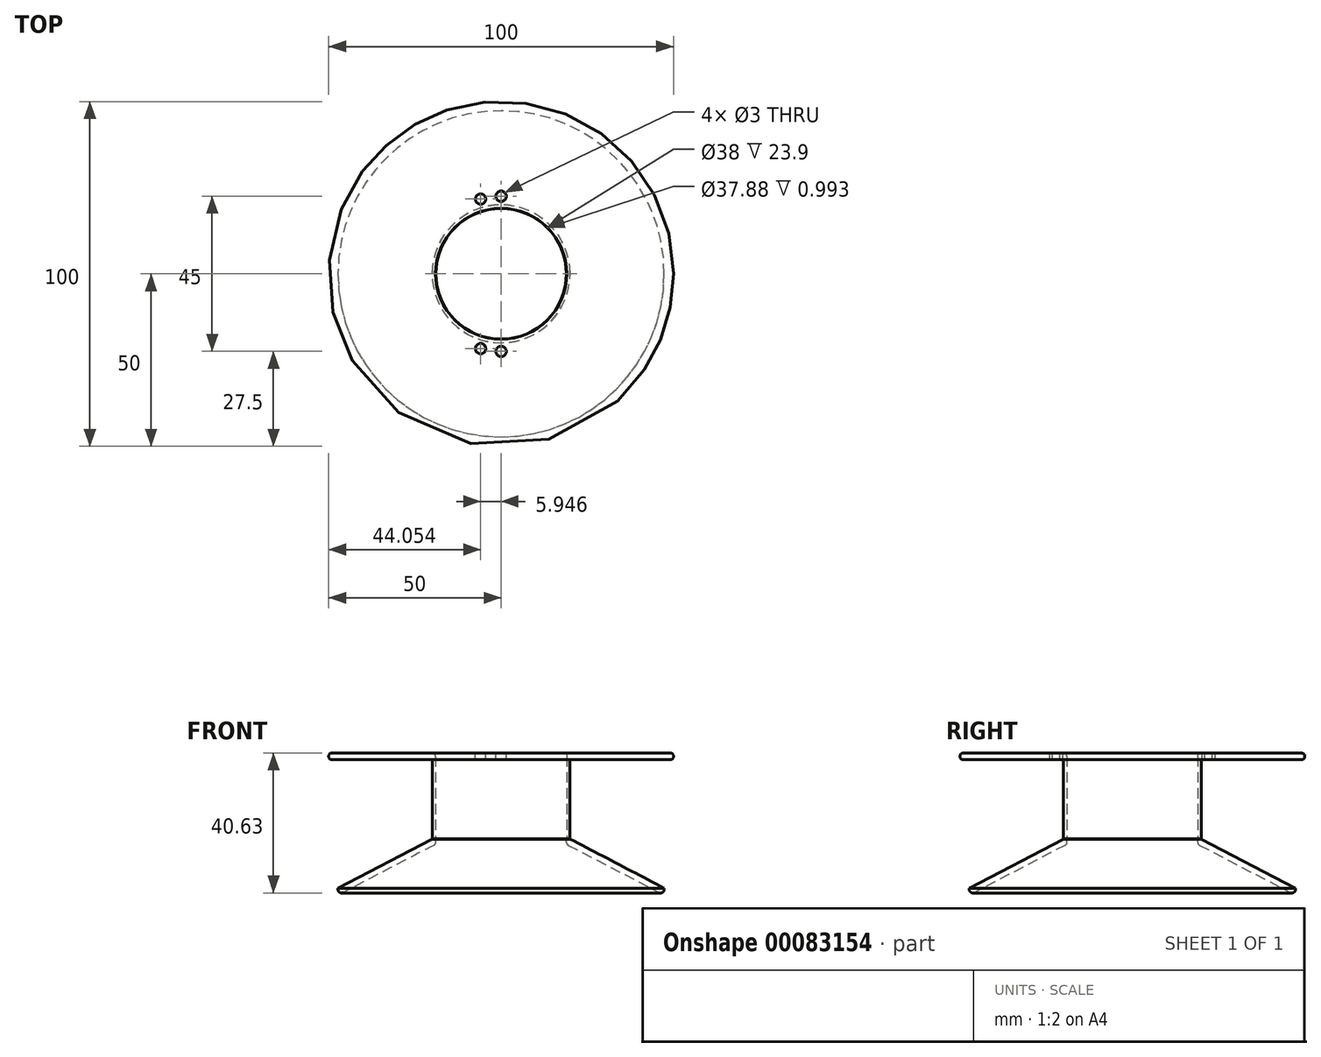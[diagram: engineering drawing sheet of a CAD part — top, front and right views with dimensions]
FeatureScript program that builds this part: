
annotation { "Feature Type Name" : "Feature", "Feature Type Description" : "" }
export const myFeature = defineFeature(function(context is Context, id is Id, definition is map)
    precondition{}
    {
        {
            var Q0;
            Q0=qCreatedBy(makeId("Top.planeOp"),FACE);
            var sketch = newSketch(context, id + "F0", { "sketchPlane" : qUnion([Q0])});
            skCircle(sketch, "E0", {"center": v(0, 0) * mm, "radius": 20 * mm});
            skCircle(sketch, "E1", {"center": v(0, 0) * mm, "radius": 19 * mm});
            skSolve(sketch);
        }
        {
            var Q0;
            Q0=makeQuery(id+"F0.imprint","IMPRINT",FACE,{"disambiguationData":[TD([[makeQuery(id+"F0.imprint","IMPRINT",EDGE,{"derivedFrom":sQuery(id+"F0.wireOp",EDGE,"E0")}),1.0]])]});
            extrude(context, id + "F1", {"entities" : qUnion([Q0]), "endBound" : BoundingType.SYMMETRIC, "depth" : 25 * mm});
        }
        {
            var Q0;
            Q0=makeQuery(id+"F1.opExtrude","CAP_FACE",FACE,{"disambiguationData":[OSD([sQuery(id+"F0.wireOp",EDGE,"E0"),sQuery(id+"F0.wireOp",EDGE,"E1")])],"isStart":false});
            var sketch = newSketch(context, id + "F2", { "sketchPlane" : qUnion([Q0])});
            skCircle(sketch, "E2", {"center": v(0, 0) * mm, "radius": 50 * mm});
            skCircle(sketch, "E3", {"center": v(0, 22.5) * mm, "radius": 1.5 * mm});
            skCircle(sketch, "E4", {"center": v(-5.95, 21.7) * mm, "radius": 1.5 * mm});
            skCircle(sketch, "E5.MirrorC", {"center": v(0, -22.5) * mm, "radius": 1.5 * mm});
            skCircle(sketch, "E6.MirrorC", {"center": v(-5.95, -21.7) * mm, "radius": 1.5 * mm});
            skSolve(sketch);
        }
        {
            var Q0;
            Q0=makeQuery(id+"F2.imprint","IMPRINT",FACE,{"disambiguationData":[TD([[makeQuery(id+"F2.imprint","IMPRINT",EDGE,{"derivedFrom":sQuery(id+"F2.wireOp",EDGE,"E2")}),1.0]])]});
            extrude(context, id + "F3", {"entities" : qUnion([Q0]), "operationType" : NewBodyOperationType.ADD, "oppositeDirection" : true, "depth" : 2 * mm});
        }
        {
            var Q0;
            Q0=qCreatedBy(makeId("Right.planeOp"),FACE);
            var sketch = newSketch(context, id + "F4", { "sketchPlane" : qUnion([Q0])});
            skLineSegment(sketch, "E7", {"start": v(-18.94, -12.5) * mm, "end": v(-18.94, -14) * mm});
            skLineSegment(sketch, "E8", {"start": v(-18.94, -12.4) * mm, "end": v(-20, -12.4) * mm});
            skLineSegment(sketch, "E9", {"start": v(-20, -12.5) * mm, "end": v(-47.3, -26.72) * mm});
            skLineSegment(sketch, "E10", {"start": v(-47.3, -26.72) * mm, "end": v(-47.3, -28.78) * mm});
            skLineSegment(sketch, "E11", {"start": v(-47.3, -28.78) * mm, "end": v(-18.94, -14) * mm});
            skLineSegment(sketch, "E12", {"start": v(0, 47.74) * mm, "end": v(0, -49.05) * mm});
            skLineSegment(sketch, "E13", {"start": v(-20, -12.4) * mm, "end": v(-20, -12.5) * mm});
            skLineSegment(sketch, "E14", {"start": v(-18.94, -12.4) * mm, "end": v(-18.94, -12.5) * mm});
            skSolve(sketch);
        }
        {
            var Q0;
            Q0=makeQuery(id+"F4.imprint","IMPRINT",FACE,{"disambiguationData":[TD([[makeQuery(id+"F4.imprint","IMPRINT",EDGE,{"derivedFrom":sQuery(id+"F4.wireOp",EDGE,"E7")}),-1.0]])]});
            var Q1;
            Q1=sQuery(id+"F4.wireOp",EDGE,"E12");
            revolve(context, id + "F5", {"operationType" : NewBodyOperationType.ADD, "entities" : qUnion([Q0]), "axis" : qUnion([Q1]), "revolveType" : RevolveType.FULL});
        }
        {
            var Q0;
            Q0=makeQuery(id+"F1.opExtrude","CAP_EDGE",EDGE,{"disambiguationData":[OSD([sQuery(id+"F0.wireOp",EDGE,"E1")])],"isStart":false});
            var Q1;
            Q1=makeQuery(id+"F3.opExtrude","CAP_EDGE",EDGE,{"disambiguationData":[OSD([sQuery(id+"F2.wireOp",EDGE,"E2")])],"isStart":true});
            var Q2;
            Q2=makeQuery(id+"F3.opExtrude","CAP_EDGE",EDGE,{"disambiguationData":[OSD([sQuery(id+"F2.wireOp",EDGE,"E2")])],"isStart":false});
            fillet(context, id + "F6", {"entities" : qUnion([Q0, Q1, Q2]), "radius" : 1 * mm, "tangentPropagation" : true, "allowEdgeOverflow" : false});
        }
        {
            var Q0;
            Q0=makeQuery(id+"F5.opRevolve","SWEPT_EDGE",EDGE,{"disambiguationData":[OSD([sQuery(id+"F4.wireOp",EDGE,"E10"),sQuery(id+"F4.wireOp",EDGE,"E11")])]});
            var Q1;
            Q1=makeQuery(id+"F5.opRevolve","SWEPT_EDGE",EDGE,{"disambiguationData":[OSD([sQuery(id+"F4.wireOp",EDGE,"E7"),sQuery(id+"F4.wireOp",EDGE,"E11")])]});
            fillet(context, id + "F7", {"entities" : qUnion([Q0, Q1]), "radius" : 1 * mm, "tangentPropagation" : true, "allowEdgeOverflow" : false});
        }
    });
